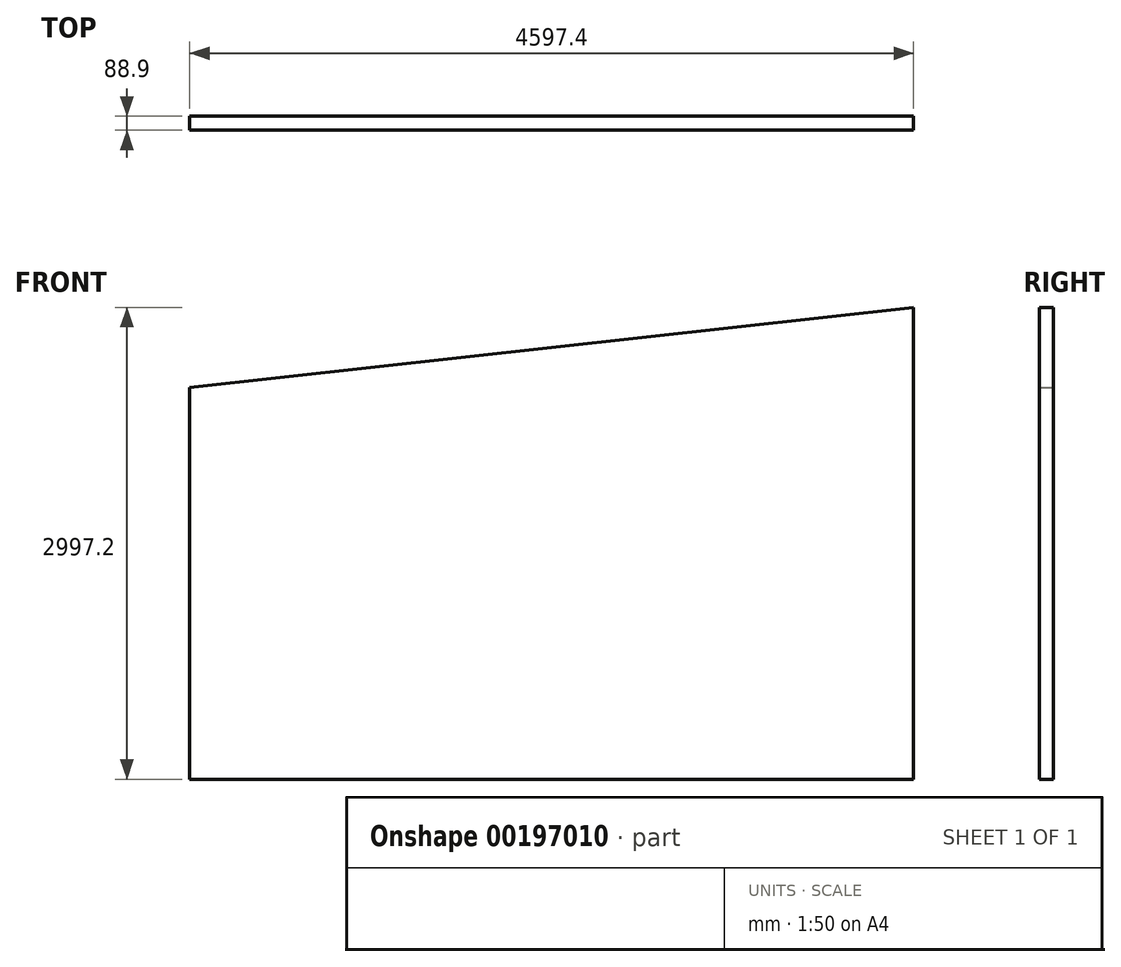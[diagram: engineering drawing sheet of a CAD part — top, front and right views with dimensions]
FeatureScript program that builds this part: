
annotation { "Feature Type Name" : "Feature", "Feature Type Description" : "" }
export const myFeature = defineFeature(function(context is Context, id is Id, definition is map)
    precondition{}
    {
        {
            var Q0;
            Q0=qCreatedBy(makeId("Front.planeOp"),FACE);
            var sketch = newSketch(context, id + "F0", { "sketchPlane" : qUnion([Q0])});
            skLineSegment(sketch, "E0", {"start": v(0, 0) * mm, "end": v(4597.4, 0) * mm});
            skLineSegment(sketch, "E1", {"start": v(0, 2489.2) * mm, "end": v(4597.4, 2997.2) * mm});
            skLineSegment(sketch, "E2", {"start": v(4597.4, 2997.2) * mm, "end": v(4597.4, 0) * mm});
            skLineSegment(sketch, "E3", {"start": v(0, 2489.2) * mm, "end": v(0, 0) * mm});
            skSolve(sketch);
        }
        {
            var Q0;
            Q0=makeQuery(id+"F0.imprint","IMPRINT",FACE,{"disambiguationData":[TD([[makeQuery(id+"F0.imprint","IMPRINT",EDGE,{"derivedFrom":sQuery(id+"F0.wireOp",EDGE,"E0")}),1.0]])]});
            extrude(context, id + "F1", {"entities" : qUnion([Q0]), "depth" : 88.9 * mm});
        }
    });
